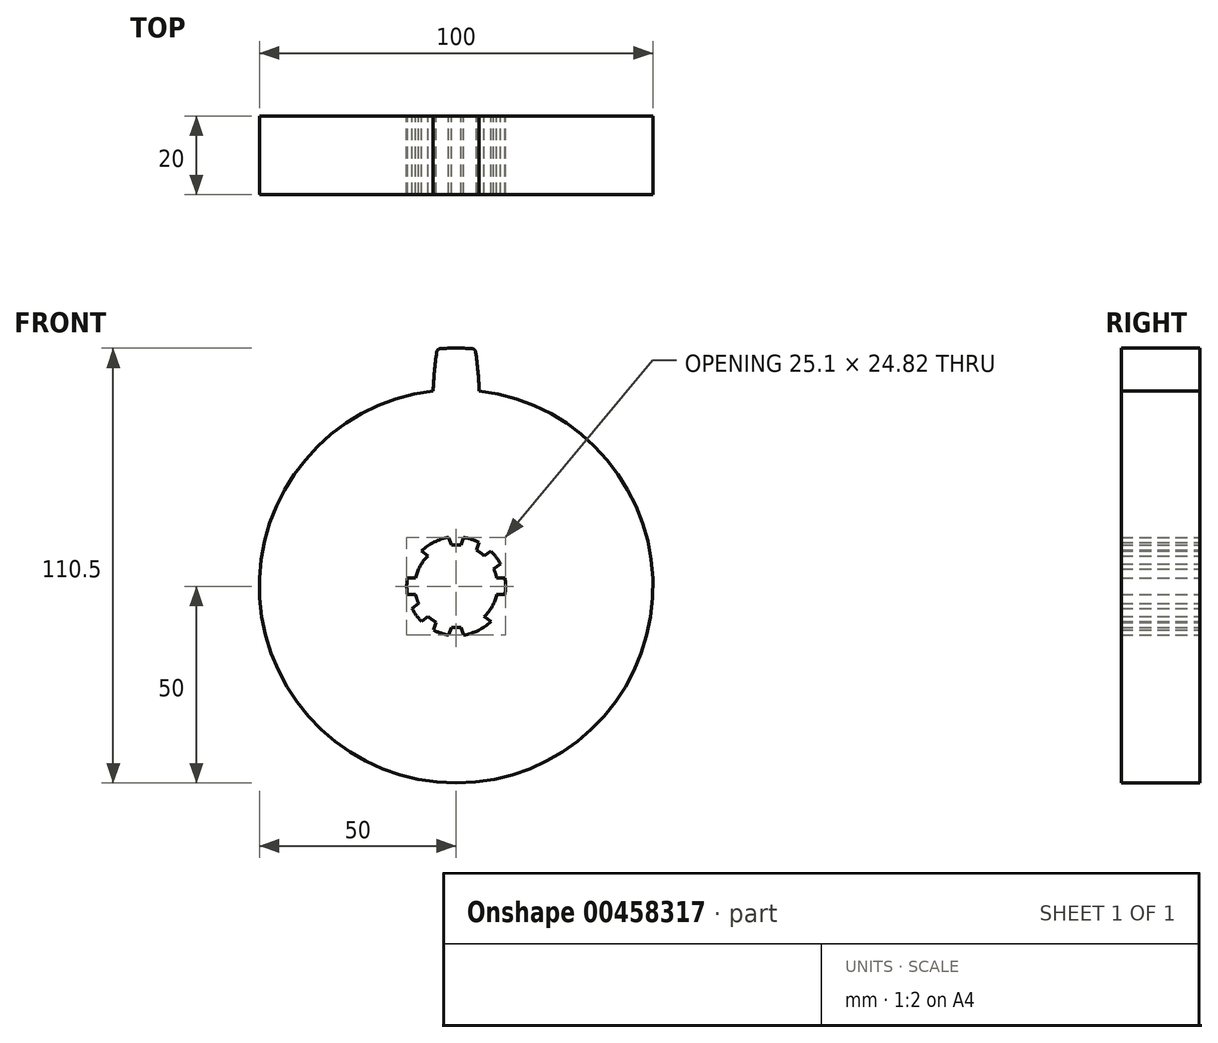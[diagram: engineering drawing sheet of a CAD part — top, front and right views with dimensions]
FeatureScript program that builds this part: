
annotation { "Feature Type Name" : "Feature", "Feature Type Description" : "" }
export const myFeature = defineFeature(function(context is Context, id is Id, definition is map)
    precondition{}
    {
        {
            var Q0;
            Q0=qCreatedBy(makeId("Front.planeOp"),FACE);
            var sketch = newSketch(context, id + "F0", { "sketchPlane" : qUnion([Q0])});
            skCircle(sketch, "E0", {"center": v(0, 0) * mm, "radius": 50 * mm});
            skCircle(sketch, "E1", {"center": v(0, 0) * mm, "radius": 12.55 * mm});
            skCircle(sketch, "E2", {"center": v(0, 0) * mm, "radius": 10.5 * mm});
            skLineSegment(sketch, "E3", {"start": v(12.38, -2.05) * mm, "end": v(-12.38, -2.05) * mm});
            skLineSegment(sketch, "E4", {"start": v(12.38, 2.05) * mm, "end": v(-12.38, 2.05) * mm});
            skLineSegment(sketch, "E5.1.0", {"start": v(1.88, 12.4) * mm, "end": v(-5.78, -11.14) * mm});
            skLineSegment(sketch, "E5.2.0", {"start": v(-11.22, 5.62) * mm, "end": v(8.81, -8.94) * mm});
            skLineSegment(sketch, "E5.3.0", {"start": v(-8.81, -8.94) * mm, "end": v(11.22, 5.62) * mm});
            skLineSegment(sketch, "E5.4.0", {"start": v(5.78, -11.14) * mm, "end": v(-1.88, 12.4) * mm});
            skLineSegment(sketch, "E6.1.0", {"start": v(5.78, 11.14) * mm, "end": v(-1.88, -12.4) * mm});
            skLineSegment(sketch, "E6.2.0", {"start": v(-8.81, 8.94) * mm, "end": v(11.22, -5.62) * mm});
            skLineSegment(sketch, "E6.3.0", {"start": v(-11.22, -5.62) * mm, "end": v(8.81, 8.94) * mm});
            skLineSegment(sketch, "E6.4.0", {"start": v(1.88, -12.4) * mm, "end": v(-5.78, 11.14) * mm});
            skSolve(sketch);
        }
        {
            var Q0;
            Q0=makeQuery(id+"F0.imprint","IMPRINT",FACE,{"disambiguationData":[TD([[makeQuery(id+"F0.imprint","IMPRINT",EDGE,{"derivedFrom":sQuery(id+"F0.wireOp",EDGE,"E0")}),1.0]])]});
            extrude(context, id + "F1", {"entities" : qUnion([Q0]), "depth" : 20 * mm, "offsetDistance" : 25 * mm});
        }
        {
            var Q0;
            {var subQ0=sQuery(id+"F0.wireOp",EDGE,"E3");var subQ1=sQuery(id+"F0.wireOp",EDGE,"E1");var subQ2=makeQuery(id+"F0.imprint","INTERSECT",VERTEX,{"disambiguationData":[OD(1.0)],"derivedFrom":[subQ1,subQ0]});Q0=makeQuery(id+"F0.imprint","IMPRINT",FACE,{"disambiguationData":[TD([[makeQuery(id+"F0.imprint","IMPRINT",EDGE,{"disambiguationData":[TD([[subQ2,-1.0]])],"derivedFrom":subQ1}),1.0]])]});}
            var Q1;
            {var subQ0=sQuery(id+"F0.wireOp",EDGE,"E4");var subQ1=sQuery(id+"F0.wireOp",EDGE,"E1");var subQ2=makeQuery(id+"F0.imprint","INTERSECT",VERTEX,{"disambiguationData":[OD(1.0)],"derivedFrom":[subQ1,subQ0]});Q1=makeQuery(id+"F0.imprint","IMPRINT",FACE,{"disambiguationData":[TD([[makeQuery(id+"F0.imprint","IMPRINT",EDGE,{"disambiguationData":[TD([[subQ2,1.0]])],"derivedFrom":subQ1}),1.0]])]});}
            var Q2;
            {var subQ0=sQuery(id+"F0.wireOp",EDGE,"E6.2.0");var subQ1=sQuery(id+"F0.wireOp",EDGE,"E1");var subQ2=makeQuery(id+"F0.imprint","INTERSECT",VERTEX,{"disambiguationData":[OD(0.0)],"derivedFrom":[subQ1,subQ0]});Q2=makeQuery(id+"F0.imprint","IMPRINT",FACE,{"disambiguationData":[TD([[makeQuery(id+"F0.imprint","IMPRINT",EDGE,{"disambiguationData":[TD([[subQ2,1.0]])],"derivedFrom":subQ1}),1.0]])]});}
            var Q3;
            {var subQ0=sQuery(id+"F0.wireOp",EDGE,"E5.1.0");var subQ1=sQuery(id+"F0.wireOp",EDGE,"E1");var subQ2=makeQuery(id+"F0.imprint","INTERSECT",VERTEX,{"disambiguationData":[OD(0.0)],"derivedFrom":[subQ1,subQ0]});Q3=makeQuery(id+"F0.imprint","IMPRINT",FACE,{"disambiguationData":[TD([[makeQuery(id+"F0.imprint","IMPRINT",EDGE,{"disambiguationData":[TD([[subQ2,-1.0]])],"derivedFrom":subQ1}),1.0]])]});}
            var Q4;
            {var subQ0=sQuery(id+"F0.wireOp",EDGE,"E6.1.0");var subQ1=sQuery(id+"F0.wireOp",EDGE,"E1");var subQ2=makeQuery(id+"F0.imprint","INTERSECT",VERTEX,{"disambiguationData":[OD(0.0)],"derivedFrom":[subQ1,subQ0]});Q4=makeQuery(id+"F0.imprint","IMPRINT",FACE,{"disambiguationData":[TD([[makeQuery(id+"F0.imprint","IMPRINT",EDGE,{"disambiguationData":[TD([[subQ2,1.0]])],"derivedFrom":subQ1}),1.0]])]});}
            var Q5;
            {var subQ0=sQuery(id+"F0.wireOp",EDGE,"E4");var subQ1=sQuery(id+"F0.wireOp",EDGE,"E1");var subQ2=makeQuery(id+"F0.imprint","INTERSECT",VERTEX,{"disambiguationData":[OD(0.0)],"derivedFrom":[subQ1,subQ0]});Q5=makeQuery(id+"F0.imprint","IMPRINT",FACE,{"disambiguationData":[TD([[makeQuery(id+"F0.imprint","IMPRINT",EDGE,{"disambiguationData":[TD([[subQ2,-1.0]])],"derivedFrom":subQ1}),1.0]])]});}
            var Q6;
            {var subQ0=sQuery(id+"F0.wireOp",EDGE,"E3");var subQ1=sQuery(id+"F0.wireOp",EDGE,"E1");var subQ2=makeQuery(id+"F0.imprint","INTERSECT",VERTEX,{"disambiguationData":[OD(0.0)],"derivedFrom":[subQ1,subQ0]});Q6=makeQuery(id+"F0.imprint","IMPRINT",FACE,{"disambiguationData":[TD([[makeQuery(id+"F0.imprint","IMPRINT",EDGE,{"disambiguationData":[TD([[subQ2,1.0]])],"derivedFrom":subQ1}),1.0]])]});}
            var Q7;
            {var subQ0=sQuery(id+"F0.wireOp",EDGE,"E5.2.0");var subQ1=sQuery(id+"F0.wireOp",EDGE,"E1");var subQ2=makeQuery(id+"F0.imprint","INTERSECT",VERTEX,{"disambiguationData":[OD(1.0)],"derivedFrom":[subQ1,subQ0]});Q7=makeQuery(id+"F0.imprint","IMPRINT",FACE,{"disambiguationData":[TD([[makeQuery(id+"F0.imprint","IMPRINT",EDGE,{"disambiguationData":[TD([[subQ2,1.0]])],"derivedFrom":subQ1}),1.0]])]});}
            var Q8;
            {var subQ0=sQuery(id+"F0.wireOp",EDGE,"E6.1.0");var subQ1=sQuery(id+"F0.wireOp",EDGE,"E1");var subQ2=makeQuery(id+"F0.imprint","INTERSECT",VERTEX,{"disambiguationData":[OD(1.0)],"derivedFrom":[subQ1,subQ0]});Q8=makeQuery(id+"F0.imprint","IMPRINT",FACE,{"disambiguationData":[TD([[makeQuery(id+"F0.imprint","IMPRINT",EDGE,{"disambiguationData":[TD([[subQ2,-1.0]])],"derivedFrom":subQ1}),1.0]])]});}
            var Q9;
            {var subQ0=sQuery(id+"F0.wireOp",EDGE,"E5.1.0");var subQ1=sQuery(id+"F0.wireOp",EDGE,"E1");var subQ2=makeQuery(id+"F0.imprint","INTERSECT",VERTEX,{"disambiguationData":[OD(1.0)],"derivedFrom":[subQ1,subQ0]});Q9=makeQuery(id+"F0.imprint","IMPRINT",FACE,{"disambiguationData":[TD([[makeQuery(id+"F0.imprint","IMPRINT",EDGE,{"disambiguationData":[TD([[subQ2,1.0]])],"derivedFrom":subQ1}),1.0]])]});}
            extrude(context, id + "F2", {"entities" : qUnion([Q0, Q1, Q2, Q3, Q4, Q5, Q6, Q7, Q8, Q9]), "operationType" : NewBodyOperationType.ADD, "depth" : 20 * mm, "offsetDistance" : 25 * mm});
        }
        {
            var Q0;
            Q0=qCreatedBy(makeId("Front.planeOp"),FACE);
            var sketch = newSketch(context, id + "F3", { "sketchPlane" : qUnion([Q0])});
            skCircle(sketch, "E7", {"center": v(0, 0) * mm, "radius": 50 * mm});
            skLineSegment(sketch, "E8", {"start": v(0, 46.5) * mm, "end": v(84.1, 46.5) * mm, "construction": true});
            skArc(sketch, "E9", {"start": v(-4.83, 60.3) * mm, "mid": v(-5.5, 55) * mm, "end": v(-5.84, 49.66) * mm});
            skArc(sketch, "E10.MirrorC", {"start": v(-4.83, 60.3) * mm, "mid": v(0, 60.5) * mm, "end": v(4.83, 60.3) * mm});
            skArc(sketch, "E11.MirrorCS", {"start": v(4.83, 60.3) * mm, "mid": v(5.5, 55) * mm, "end": v(5.84, 49.66) * mm});
            skArc(sketch, "E12.1.0", {"start": v(-20.11, 57.06) * mm, "mid": v(-17.35, 52.48) * mm, "end": v(-14.86, 47.74) * mm});
            skArc(sketch, "E12.1.1", {"start": v(-28.95, 53.13) * mm, "mid": v(-24.6, 55.27) * mm, "end": v(-20.11, 57.06) * mm});
            skArc(sketch, "E12.1.2", {"start": v(-28.95, 53.13) * mm, "mid": v(-27.4, 48) * mm, "end": v(-25.54, 42.99) * mm});
            skArc(sketch, "E12.2.0", {"start": v(-41.58, 43.95) * mm, "mid": v(-37.2, 40.89) * mm, "end": v(-33, 37.57) * mm});
            skArc(sketch, "E12.2.1", {"start": v(-48.05, 36.76) * mm, "mid": v(-44.96, 40.48) * mm, "end": v(-41.58, 43.95) * mm});
            skArc(sketch, "E12.2.2", {"start": v(-48.05, 36.76) * mm, "mid": v(-44.55, 32.71) * mm, "end": v(-40.81, 28.88) * mm});
            skArc(sketch, "E12.3.0", {"start": v(-55.86, 23.23) * mm, "mid": v(-50.6, 22.22) * mm, "end": v(-45.42, 20.9) * mm});
            skArc(sketch, "E12.3.1", {"start": v(-58.85, 14.04) * mm, "mid": v(-57.54, 18.7) * mm, "end": v(-55.86, 23.23) * mm});
            skArc(sketch, "E12.3.2", {"start": v(-58.85, 14.04) * mm, "mid": v(-54, 11.77) * mm, "end": v(-49.03, 9.79) * mm});
            skArc(sketch, "E12.4.0", {"start": v(-60.48, -1.5) * mm, "mid": v(-55.27, -0.28) * mm, "end": v(-50, 0.62) * mm});
            skArc(sketch, "E12.4.1", {"start": v(-59.47, -11.11) * mm, "mid": v(-60.17, -6.32) * mm, "end": v(-60.48, -1.5) * mm});
            skArc(sketch, "E12.4.2", {"start": v(-59.47, -11.11) * mm, "mid": v(-54.12, -11.22) * mm, "end": v(-48.77, -11) * mm});
            skArc(sketch, "E12.5.0", {"start": v(-54.64, -25.97) * mm, "mid": v(-50.38, -22.74) * mm, "end": v(-45.93, -19.77) * mm});
            skArc(sketch, "E12.5.1", {"start": v(-49.8, -34.34) * mm, "mid": v(-52.4, -30.25) * mm, "end": v(-54.64, -25.97) * mm});
            skArc(sketch, "E12.5.2", {"start": v(-49.8, -34.34) * mm, "mid": v(-44.88, -32.26) * mm, "end": v(-40.08, -29.9) * mm});
            skArc(sketch, "E12.6.0", {"start": v(-39.36, -45.95) * mm, "mid": v(-36.77, -41.26) * mm, "end": v(-33.92, -36.74) * mm});
            skArc(sketch, "E12.6.1", {"start": v(-31.54, -51.63) * mm, "mid": v(-35.56, -48.95) * mm, "end": v(-39.36, -45.95) * mm});
            skArc(sketch, "E12.6.2", {"start": v(-31.54, -51.63) * mm, "mid": v(-27.88, -47.73) * mm, "end": v(-24.46, -43.6) * mm});
            skArc(sketch, "E12.7.0", {"start": v(-17.27, -57.98) * mm, "mid": v(-16.81, -52.65) * mm, "end": v(-16.04, -47.36) * mm});
            skArc(sketch, "E12.7.1", {"start": v(-7.8, -60) * mm, "mid": v(-12.58, -59.18) * mm, "end": v(-17.27, -57.98) * mm});
            skArc(sketch, "E12.7.2", {"start": v(-7.8, -60) * mm, "mid": v(-6.06, -54.94) * mm, "end": v(-4.6, -49.79) * mm});
            skArc(sketch, "E12.8.0", {"start": v(7.8, -60) * mm, "mid": v(6.06, -54.94) * mm, "end": v(4.6, -49.79) * mm});
            skArc(sketch, "E12.8.1", {"start": v(17.27, -57.98) * mm, "mid": v(12.58, -59.18) * mm, "end": v(7.8, -60) * mm});
            skArc(sketch, "E12.8.2", {"start": v(17.27, -57.98) * mm, "mid": v(16.81, -52.65) * mm, "end": v(16.04, -47.36) * mm});
            skArc(sketch, "E12.9.0", {"start": v(31.54, -51.63) * mm, "mid": v(27.88, -47.73) * mm, "end": v(24.46, -43.6) * mm});
            skArc(sketch, "E12.9.1", {"start": v(39.36, -45.95) * mm, "mid": v(35.56, -48.95) * mm, "end": v(31.54, -51.63) * mm});
            skArc(sketch, "E12.9.2", {"start": v(39.36, -45.95) * mm, "mid": v(36.77, -41.26) * mm, "end": v(33.92, -36.74) * mm});
            skArc(sketch, "E12.10.0", {"start": v(49.8, -34.34) * mm, "mid": v(44.88, -32.26) * mm, "end": v(40.08, -29.9) * mm});
            skArc(sketch, "E12.10.1", {"start": v(54.64, -25.97) * mm, "mid": v(52.4, -30.25) * mm, "end": v(49.8, -34.34) * mm});
            skArc(sketch, "E12.10.2", {"start": v(54.64, -25.97) * mm, "mid": v(50.38, -22.74) * mm, "end": v(45.93, -19.77) * mm});
            skArc(sketch, "E12.11.0", {"start": v(59.47, -11.11) * mm, "mid": v(54.12, -11.22) * mm, "end": v(48.77, -11) * mm});
            skArc(sketch, "E12.11.1", {"start": v(60.48, -1.5) * mm, "mid": v(60.17, -6.32) * mm, "end": v(59.47, -11.11) * mm});
            skArc(sketch, "E12.11.2", {"start": v(60.48, -1.5) * mm, "mid": v(55.27, -0.28) * mm, "end": v(50, 0.62) * mm});
            skArc(sketch, "E12.12.0", {"start": v(58.85, 14.04) * mm, "mid": v(54, 11.77) * mm, "end": v(49.03, 9.79) * mm});
            skArc(sketch, "E12.12.1", {"start": v(55.86, 23.23) * mm, "mid": v(57.54, 18.7) * mm, "end": v(58.85, 14.04) * mm});
            skArc(sketch, "E12.12.2", {"start": v(55.86, 23.23) * mm, "mid": v(50.6, 22.22) * mm, "end": v(45.42, 20.9) * mm});
            skArc(sketch, "E12.13.0", {"start": v(48.05, 36.76) * mm, "mid": v(44.55, 32.71) * mm, "end": v(40.81, 28.88) * mm});
            skArc(sketch, "E12.13.1", {"start": v(41.58, 43.95) * mm, "mid": v(44.96, 40.48) * mm, "end": v(48.05, 36.76) * mm});
            skArc(sketch, "E12.13.2", {"start": v(41.58, 43.95) * mm, "mid": v(37.2, 40.89) * mm, "end": v(33, 37.57) * mm});
            skArc(sketch, "E12.14.0", {"start": v(28.95, 53.13) * mm, "mid": v(27.4, 48) * mm, "end": v(25.54, 42.99) * mm});
            skArc(sketch, "E12.14.1", {"start": v(20.11, 57.06) * mm, "mid": v(24.6, 55.27) * mm, "end": v(28.95, 53.13) * mm});
            skArc(sketch, "E12.14.2", {"start": v(20.11, 57.06) * mm, "mid": v(17.35, 52.48) * mm, "end": v(14.86, 47.74) * mm});
            skSolve(sketch);
        }
        {
            var Q0;
            {var subQ0=sQuery(id+"F3.wireOp",EDGE,"E9");Q0=makeQuery(id+"F3.imprint","IMPRINT",FACE,{"disambiguationData":[TD([[makeQuery(id+"F3.imprint","IMPRINT",EDGE,{"derivedFrom":subQ0}),1.0]])]});}
            var Q1;
            {var subQ0=sQuery(id+"F3.wireOp",EDGE,"E12.14.0");Q1=makeQuery(id+"F3.imprint","IMPRINT",FACE,{"disambiguationData":[TD([[makeQuery(id+"F3.imprint","IMPRINT",EDGE,{"derivedFrom":subQ0}),-1.0]])]});}
            var Q2;
            {var subQ0=sQuery(id+"F3.wireOp",EDGE,"E12.13.0");Q2=makeQuery(id+"F3.imprint","IMPRINT",FACE,{"disambiguationData":[TD([[makeQuery(id+"F3.imprint","IMPRINT",EDGE,{"derivedFrom":subQ0}),-1.0]])]});}
            var Q3;
            {var subQ0=sQuery(id+"F3.wireOp",EDGE,"E12.12.0");Q3=makeQuery(id+"F3.imprint","IMPRINT",FACE,{"disambiguationData":[TD([[makeQuery(id+"F3.imprint","IMPRINT",EDGE,{"derivedFrom":subQ0}),-1.0]])]});}
            var Q4;
            {var subQ0=sQuery(id+"F3.wireOp",EDGE,"E12.11.0");Q4=makeQuery(id+"F3.imprint","IMPRINT",FACE,{"disambiguationData":[TD([[makeQuery(id+"F3.imprint","IMPRINT",EDGE,{"derivedFrom":subQ0}),-1.0]])]});}
            var Q5;
            {var subQ0=sQuery(id+"F3.wireOp",EDGE,"E12.10.0");Q5=makeQuery(id+"F3.imprint","IMPRINT",FACE,{"disambiguationData":[TD([[makeQuery(id+"F3.imprint","IMPRINT",EDGE,{"derivedFrom":subQ0}),-1.0]])]});}
            var Q6;
            {var subQ0=sQuery(id+"F3.wireOp",EDGE,"E12.9.0");Q6=makeQuery(id+"F3.imprint","IMPRINT",FACE,{"disambiguationData":[TD([[makeQuery(id+"F3.imprint","IMPRINT",EDGE,{"derivedFrom":subQ0}),-1.0]])]});}
            var Q7;
            {var subQ0=sQuery(id+"F3.wireOp",EDGE,"E12.8.0");Q7=makeQuery(id+"F3.imprint","IMPRINT",FACE,{"disambiguationData":[TD([[makeQuery(id+"F3.imprint","IMPRINT",EDGE,{"derivedFrom":subQ0}),-1.0]])]});}
            var Q8;
            {var subQ0=sQuery(id+"F3.wireOp",EDGE,"E12.7.0");Q8=makeQuery(id+"F3.imprint","IMPRINT",FACE,{"disambiguationData":[TD([[makeQuery(id+"F3.imprint","IMPRINT",EDGE,{"derivedFrom":subQ0}),-1.0]])]});}
            var Q9;
            {var subQ0=sQuery(id+"F3.wireOp",EDGE,"E12.6.0");Q9=makeQuery(id+"F3.imprint","IMPRINT",FACE,{"disambiguationData":[TD([[makeQuery(id+"F3.imprint","IMPRINT",EDGE,{"derivedFrom":subQ0}),-1.0]])]});}
            var Q10;
            {var subQ0=sQuery(id+"F3.wireOp",EDGE,"E12.5.0");Q10=makeQuery(id+"F3.imprint","IMPRINT",FACE,{"disambiguationData":[TD([[makeQuery(id+"F3.imprint","IMPRINT",EDGE,{"derivedFrom":subQ0}),-1.0]])]});}
            var Q11;
            {var subQ0=sQuery(id+"F3.wireOp",EDGE,"E12.4.0");Q11=makeQuery(id+"F3.imprint","IMPRINT",FACE,{"disambiguationData":[TD([[makeQuery(id+"F3.imprint","IMPRINT",EDGE,{"derivedFrom":subQ0}),-1.0]])]});}
            var Q12;
            {var subQ0=sQuery(id+"F3.wireOp",EDGE,"E12.1.0");Q12=makeQuery(id+"F3.imprint","IMPRINT",FACE,{"disambiguationData":[TD([[makeQuery(id+"F3.imprint","IMPRINT",EDGE,{"derivedFrom":subQ0}),-1.0]])]});}
            var Q13;
            {var subQ0=sQuery(id+"F3.wireOp",EDGE,"E12.2.0");Q13=makeQuery(id+"F3.imprint","IMPRINT",FACE,{"disambiguationData":[TD([[makeQuery(id+"F3.imprint","IMPRINT",EDGE,{"derivedFrom":subQ0}),-1.0]])]});}
            var Q14;
            {var subQ0=sQuery(id+"F3.wireOp",EDGE,"E12.3.0");Q14=makeQuery(id+"F3.imprint","IMPRINT",FACE,{"disambiguationData":[TD([[makeQuery(id+"F3.imprint","IMPRINT",EDGE,{"derivedFrom":subQ0}),-1.0]])]});}
            extrude(context, id + "F4", {"entities" : qUnion([Q0, Q1, Q2, Q3, Q4, Q5, Q6, Q7, Q8, Q9, Q10, Q11, Q12, Q13, Q14]), "operationType" : NewBodyOperationType.ADD, "depth" : 20 * mm, "offsetDistance" : 25 * mm});
        }
        {
            var Q0;
            Q0=makeQuery(id+"F4.opExtrude","SWEPT_EDGE",EDGE,{"disambiguationData":[OSD([sQuery(id+"F3.wireOp",EDGE,"E12.6.1"),sQuery(id+"F3.wireOp",EDGE,"E12.6.2")])]});
            var Q1;
            Q1=makeQuery(id+"F4.opExtrude","SWEPT_EDGE",EDGE,{"disambiguationData":[OSD([sQuery(id+"F3.wireOp",EDGE,"E12.7.0"),sQuery(id+"F3.wireOp",EDGE,"E12.7.1")])]});
            var Q2;
            Q2=makeQuery(id+"F4.opExtrude","SWEPT_EDGE",EDGE,{"disambiguationData":[OSD([sQuery(id+"F3.wireOp",EDGE,"E12.7.1"),sQuery(id+"F3.wireOp",EDGE,"E12.7.2")])]});
            var Q3;
            Q3=makeQuery(id+"F4.opExtrude","SWEPT_EDGE",EDGE,{"disambiguationData":[OSD([sQuery(id+"F3.wireOp",EDGE,"E12.8.0"),sQuery(id+"F3.wireOp",EDGE,"E12.8.1")])]});
            var Q4;
            Q4=makeQuery(id+"F4.opExtrude","SWEPT_EDGE",EDGE,{"disambiguationData":[OSD([sQuery(id+"F3.wireOp",EDGE,"E12.8.1"),sQuery(id+"F3.wireOp",EDGE,"E12.8.2")])]});
            var Q5;
            Q5=makeQuery(id+"F4.opExtrude","SWEPT_EDGE",EDGE,{"disambiguationData":[OSD([sQuery(id+"F3.wireOp",EDGE,"E12.9.0"),sQuery(id+"F3.wireOp",EDGE,"E12.9.1")])]});
            var Q6;
            Q6=makeQuery(id+"F4.opExtrude","SWEPT_EDGE",EDGE,{"disambiguationData":[OSD([sQuery(id+"F3.wireOp",EDGE,"E12.9.1"),sQuery(id+"F3.wireOp",EDGE,"E12.9.2")])]});
            var Q7;
            Q7=makeQuery(id+"F4.opExtrude","SWEPT_EDGE",EDGE,{"disambiguationData":[OSD([sQuery(id+"F3.wireOp",EDGE,"E12.10.0"),sQuery(id+"F3.wireOp",EDGE,"E12.10.1")])]});
            var Q8;
            Q8=makeQuery(id+"F4.opExtrude","SWEPT_EDGE",EDGE,{"disambiguationData":[OSD([sQuery(id+"F3.wireOp",EDGE,"E12.10.1"),sQuery(id+"F3.wireOp",EDGE,"E12.10.2")])]});
            var Q9;
            Q9=makeQuery(id+"F4.opExtrude","SWEPT_EDGE",EDGE,{"disambiguationData":[OSD([sQuery(id+"F3.wireOp",EDGE,"E12.11.0"),sQuery(id+"F3.wireOp",EDGE,"E12.11.1")])]});
            var Q10;
            Q10=makeQuery(id+"F4.opExtrude","SWEPT_EDGE",EDGE,{"disambiguationData":[OSD([sQuery(id+"F3.wireOp",EDGE,"E12.11.1"),sQuery(id+"F3.wireOp",EDGE,"E12.11.2")])]});
            var Q11;
            Q11=makeQuery(id+"F4.opExtrude","SWEPT_EDGE",EDGE,{"disambiguationData":[OSD([sQuery(id+"F3.wireOp",EDGE,"E12.12.0"),sQuery(id+"F3.wireOp",EDGE,"E12.12.1")])]});
            var Q12;
            Q12=makeQuery(id+"F4.opExtrude","SWEPT_EDGE",EDGE,{"disambiguationData":[OSD([sQuery(id+"F3.wireOp",EDGE,"E12.12.1"),sQuery(id+"F3.wireOp",EDGE,"E12.12.2")])]});
            var Q13;
            Q13=makeQuery(id+"F4.opExtrude","SWEPT_EDGE",EDGE,{"disambiguationData":[OSD([sQuery(id+"F3.wireOp",EDGE,"E12.13.0"),sQuery(id+"F3.wireOp",EDGE,"E12.13.1")])]});
            var Q14;
            Q14=makeQuery(id+"F4.opExtrude","SWEPT_EDGE",EDGE,{"disambiguationData":[OSD([sQuery(id+"F3.wireOp",EDGE,"E12.13.1"),sQuery(id+"F3.wireOp",EDGE,"E12.13.2")])]});
            var Q15;
            Q15=makeQuery(id+"F4.opExtrude","SWEPT_EDGE",EDGE,{"disambiguationData":[OSD([sQuery(id+"F3.wireOp",EDGE,"E12.14.0"),sQuery(id+"F3.wireOp",EDGE,"E12.14.1")])]});
            var Q16;
            Q16=makeQuery(id+"F4.opExtrude","SWEPT_EDGE",EDGE,{"disambiguationData":[OSD([sQuery(id+"F3.wireOp",EDGE,"E12.14.1"),sQuery(id+"F3.wireOp",EDGE,"E12.14.2")])]});
            var Q17;
            Q17=makeQuery(id+"F4.opExtrude","SWEPT_EDGE",EDGE,{"disambiguationData":[OSD([sQuery(id+"F3.wireOp",EDGE,"E10.MirrorC"),sQuery(id+"F3.wireOp",EDGE,"E11.MirrorCS")])]});
            var Q18;
            Q18=makeQuery(id+"F4.opExtrude","SWEPT_EDGE",EDGE,{"disambiguationData":[OSD([sQuery(id+"F3.wireOp",EDGE,"E9"),sQuery(id+"F3.wireOp",EDGE,"E10.MirrorC")])]});
            var Q19;
            Q19=makeQuery(id+"F4.opExtrude","SWEPT_EDGE",EDGE,{"disambiguationData":[OSD([sQuery(id+"F3.wireOp",EDGE,"E12.1.0"),sQuery(id+"F3.wireOp",EDGE,"E12.1.1")])]});
            var Q20;
            Q20=makeQuery(id+"F4.opExtrude","SWEPT_EDGE",EDGE,{"disambiguationData":[OSD([sQuery(id+"F3.wireOp",EDGE,"E12.2.0"),sQuery(id+"F3.wireOp",EDGE,"E12.2.1")])]});
            var Q21;
            Q21=makeQuery(id+"F4.opExtrude","SWEPT_EDGE",EDGE,{"disambiguationData":[OSD([sQuery(id+"F3.wireOp",EDGE,"E12.2.1"),sQuery(id+"F3.wireOp",EDGE,"E12.2.2")])]});
            var Q22;
            Q22=makeQuery(id+"F4.opExtrude","SWEPT_EDGE",EDGE,{"disambiguationData":[OSD([sQuery(id+"F3.wireOp",EDGE,"E12.3.0"),sQuery(id+"F3.wireOp",EDGE,"E12.3.1")])]});
            var Q23;
            Q23=makeQuery(id+"F4.opExtrude","SWEPT_EDGE",EDGE,{"disambiguationData":[OSD([sQuery(id+"F3.wireOp",EDGE,"E12.3.1"),sQuery(id+"F3.wireOp",EDGE,"E12.3.2")])]});
            var Q24;
            Q24=makeQuery(id+"F4.opExtrude","SWEPT_EDGE",EDGE,{"disambiguationData":[OSD([sQuery(id+"F3.wireOp",EDGE,"E12.4.0"),sQuery(id+"F3.wireOp",EDGE,"E12.4.1")])]});
            var Q25;
            Q25=makeQuery(id+"F4.opExtrude","SWEPT_EDGE",EDGE,{"disambiguationData":[OSD([sQuery(id+"F3.wireOp",EDGE,"E12.4.1"),sQuery(id+"F3.wireOp",EDGE,"E12.4.2")])]});
            var Q26;
            Q26=makeQuery(id+"F4.opExtrude","SWEPT_EDGE",EDGE,{"disambiguationData":[OSD([sQuery(id+"F3.wireOp",EDGE,"E12.5.0"),sQuery(id+"F3.wireOp",EDGE,"E12.5.1")])]});
            var Q27;
            Q27=makeQuery(id+"F4.opExtrude","SWEPT_EDGE",EDGE,{"disambiguationData":[OSD([sQuery(id+"F3.wireOp",EDGE,"E12.5.1"),sQuery(id+"F3.wireOp",EDGE,"E12.5.2")])]});
            var Q28;
            Q28=makeQuery(id+"F4.opExtrude","SWEPT_EDGE",EDGE,{"disambiguationData":[OSD([sQuery(id+"F3.wireOp",EDGE,"E12.6.0"),sQuery(id+"F3.wireOp",EDGE,"E12.6.1")])]});
            fillet(context, id + "F5", {"entities" : qUnion([Q0, Q1, Q2, Q3, Q4, Q5, Q6, Q7, Q8, Q9, Q10, Q11, Q12, Q13, Q14, Q15, Q16, Q17, Q18, Q19, Q20, Q21, Q22, Q23, Q24, Q25, Q26, Q27, Q28]), "radius" : 1 * mm, "tangentPropagation" : true, "allowEdgeOverflow" : false});
        }
    });
